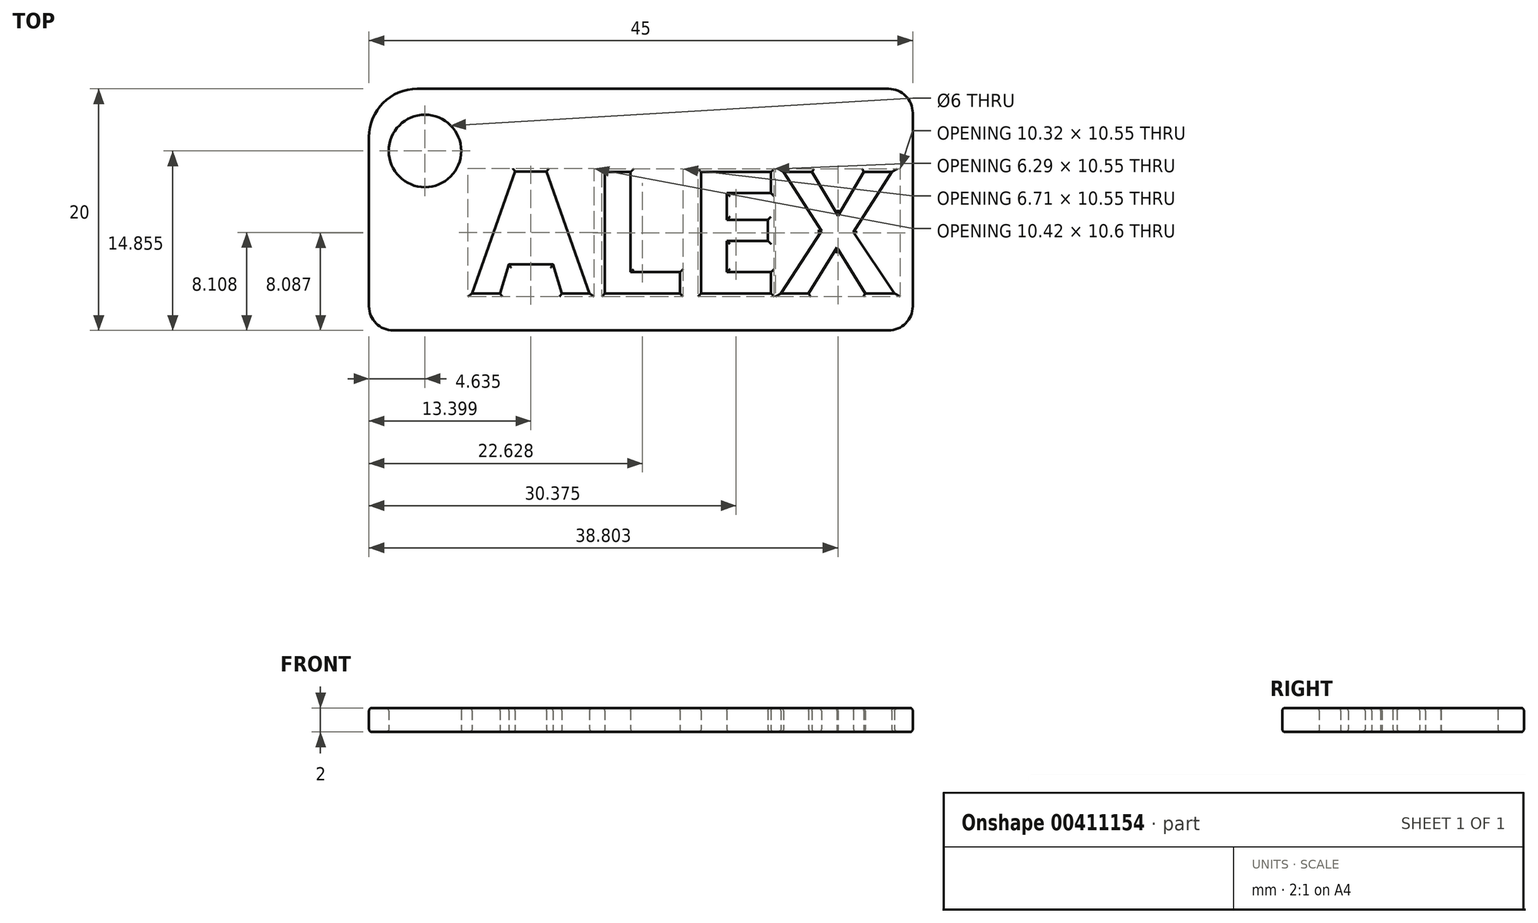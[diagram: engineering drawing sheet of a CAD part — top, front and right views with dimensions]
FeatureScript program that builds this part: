
annotation { "Feature Type Name" : "Feature", "Feature Type Description" : "" }
export const myFeature = defineFeature(function(context is Context, id is Id, definition is map)
    precondition{}
    {
        {
            var Q0;
            Q0=qCreatedBy(makeId("Top.planeOp"),FACE);
            var sketch = newSketch(context, id + "F0", { "sketchPlane" : qUnion([Q0])});
            skLineSegment(sketch, "E0.bottom", {"start": v(4, 0) * mm, "end": v(43, 0) * mm});
            skLineSegment(sketch, "E0.top", {"start": v(2, -20) * mm, "end": v(43, -20) * mm});
            skLineSegment(sketch, "E0.left", {"start": v(0, -4) * mm, "end": v(0, -18) * mm});
            skLineSegment(sketch, "E0.right", {"start": v(45, -2) * mm, "end": v(45, -18) * mm});
            skCircle(sketch, "E1", {"center": v(4.63, -5.15) * mm, "radius": 3 * mm});
            skText(sketch, "E2", { "text": "ALEX", "fontName": "OpenSans-Bold.ttf"});
            skPoint(sketch, "E3.visualSharp", {"position": v(0, 0) * mm});
            skArc(sketch, "E3.filletArc", {"start": v(4, 0) * mm, "mid": v(1.17, -1.17) * mm, "end": v(0, -4) * mm});
            skPoint(sketch, "E4.visualSharp", {"position": v(0, -20) * mm});
            skArc(sketch, "E4.filletArc", {"start": v(0, -18) * mm, "mid": v(0.59, -19.41) * mm, "end": v(2, -20) * mm});
            skPoint(sketch, "E5.visualSharp", {"position": v(45, -20) * mm});
            skArc(sketch, "E5.filletArc", {"start": v(43, -20) * mm, "mid": v(44.41, -19.41) * mm, "end": v(45, -18) * mm});
            skPoint(sketch, "E6.visualSharp", {"position": v(45, 0) * mm});
            skArc(sketch, "E6.filletArc", {"start": v(45, -2) * mm, "mid": v(44.41, -0.59) * mm, "end": v(43, 0) * mm});
            skLineSegment(sketch, "E7", {"start": v(12, -6.8) * mm, "end": v(13.42, -8.68) * mm});
            const initialGuessF0  = {"E2": [0.00854, -0.01694, 1, 0, 0.01014]};
            skSetInitialGuess(sketch, initialGuessF0);
            skSolve(sketch);
        }
        {
            var Q0;
            Q0=makeQuery(id+"F0.imprint","IMPRINT",FACE,{"disambiguationData":[TD([[makeQuery(id+"F0.imprint","IMPRINT",EDGE,{"derivedFrom":sQuery(id+"F0.wireOp",EDGE,"E0.bottom")}),-1.0]])]});
            extrude(context, id + "F1", {"entities" : qUnion([Q0]), "depth" : 2 * mm});
        }
        {
            var Q0;
            Q0=makeQuery(id+"F1.opExtrude","CAP_FACE",FACE,{"disambiguationData":[OSD([sQuery(id+"F0.wireOp",EDGE,"E0.bottom"),sQuery(id+"F0.wireOp",EDGE,"E0.top"),sQuery(id+"F0.wireOp",EDGE,"E0.left"),sQuery(id+"F0.wireOp",EDGE,"E0.right"),sQuery(id+"F0.wireOp",EDGE,"E1"),sQuery(id+"F0.wireOp",EDGE,"E2.sketch_text.stroke-0"),sQuery(id+"F0.wireOp",EDGE,"E2.sketch_text.stroke-1"),sQuery(id+"F0.wireOp",EDGE,"E2.sketch_text.stroke-2"),sQuery(id+"F0.wireOp",EDGE,"E2.sketch_text.stroke-3"),sQuery(id+"F0.wireOp",EDGE,"E2.sketch_text.stroke-4"),sQuery(id+"F0.wireOp",EDGE,"E2.sketch_text.stroke-5"),sQuery(id+"F0.wireOp",EDGE,"E2.sketch_text.stroke-6"),sQuery(id+"F0.wireOp",EDGE,"E2.sketch_text.stroke-7"),sQuery(id+"F0.wireOp",EDGE,"E2.sketch_text.stroke-12"),sQuery(id+"F0.wireOp",EDGE,"E2.sketch_text.stroke-13"),sQuery(id+"F0.wireOp",EDGE,"E2.sketch_text.stroke-14"),sQuery(id+"F0.wireOp",EDGE,"E2.sketch_text.stroke-15"),sQuery(id+"F0.wireOp",EDGE,"E2.sketch_text.stroke-16"),sQuery(id+"F0.wireOp",EDGE,"E2.sketch_text.stroke-17"),sQuery(id+"F0.wireOp",EDGE,"E2.sketch_text.stroke-18"),sQuery(id+"F0.wireOp",EDGE,"E2.sketch_text.stroke-19"),sQuery(id+"F0.wireOp",EDGE,"E2.sketch_text.stroke-20"),sQuery(id+"F0.wireOp",EDGE,"E2.sketch_text.stroke-21"),sQuery(id+"F0.wireOp",EDGE,"E2.sketch_text.stroke-22"),sQuery(id+"F0.wireOp",EDGE,"E2.sketch_text.stroke-23"),sQuery(id+"F0.wireOp",EDGE,"E2.sketch_text.stroke-24"),sQuery(id+"F0.wireOp",EDGE,"E2.sketch_text.stroke-25"),sQuery(id+"F0.wireOp",EDGE,"E2.sketch_text.stroke-26"),sQuery(id+"F0.wireOp",EDGE,"E2.sketch_text.stroke-27"),sQuery(id+"F0.wireOp",EDGE,"E2.sketch_text.stroke-28"),sQuery(id+"F0.wireOp",EDGE,"E2.sketch_text.stroke-29"),sQuery(id+"F0.wireOp",EDGE,"E2.sketch_text.stroke-30"),sQuery(id+"F0.wireOp",EDGE,"E2.sketch_text.stroke-31"),sQuery(id+"F0.wireOp",EDGE,"E2.sketch_text.stroke-32"),sQuery(id+"F0.wireOp",EDGE,"E2.sketch_text.stroke-33"),sQuery(id+"F0.wireOp",EDGE,"E2.sketch_text.stroke-34"),sQuery(id+"F0.wireOp",EDGE,"E2.sketch_text.stroke-35"),sQuery(id+"F0.wireOp",EDGE,"E2.sketch_text.stroke-36"),sQuery(id+"F0.wireOp",EDGE,"E2.sketch_text.stroke-37"),sQuery(id+"F0.wireOp",EDGE,"E2.sketch_text.stroke-38"),sQuery(id+"F0.wireOp",EDGE,"E2.sketch_text.stroke-39"),sQuery(id+"F0.wireOp",EDGE,"E2.sketch_text.stroke-40"),sQuery(id+"F0.wireOp",EDGE,"E2.sketch_text.stroke-41"),sQuery(id+"F0.wireOp",EDGE,"E3.filletArc"),sQuery(id+"F0.wireOp",EDGE,"E4.filletArc"),sQuery(id+"F0.wireOp",EDGE,"E5.filletArc"),sQuery(id+"F0.wireOp",EDGE,"E6.filletArc")])],"isStart":false});
            var Q1;
            Q1=makeQuery(id+"F1.opExtrude","CAP_FACE",FACE,{"disambiguationData":[OSD([sQuery(id+"F0.wireOp",EDGE,"E0.bottom"),sQuery(id+"F0.wireOp",EDGE,"E0.top"),sQuery(id+"F0.wireOp",EDGE,"E0.left"),sQuery(id+"F0.wireOp",EDGE,"E0.right"),sQuery(id+"F0.wireOp",EDGE,"E1"),sQuery(id+"F0.wireOp",EDGE,"E2.sketch_text.stroke-0"),sQuery(id+"F0.wireOp",EDGE,"E2.sketch_text.stroke-1"),sQuery(id+"F0.wireOp",EDGE,"E2.sketch_text.stroke-2"),sQuery(id+"F0.wireOp",EDGE,"E2.sketch_text.stroke-3"),sQuery(id+"F0.wireOp",EDGE,"E2.sketch_text.stroke-4"),sQuery(id+"F0.wireOp",EDGE,"E2.sketch_text.stroke-5"),sQuery(id+"F0.wireOp",EDGE,"E2.sketch_text.stroke-6"),sQuery(id+"F0.wireOp",EDGE,"E2.sketch_text.stroke-7"),sQuery(id+"F0.wireOp",EDGE,"E2.sketch_text.stroke-12"),sQuery(id+"F0.wireOp",EDGE,"E2.sketch_text.stroke-13"),sQuery(id+"F0.wireOp",EDGE,"E2.sketch_text.stroke-14"),sQuery(id+"F0.wireOp",EDGE,"E2.sketch_text.stroke-15"),sQuery(id+"F0.wireOp",EDGE,"E2.sketch_text.stroke-16"),sQuery(id+"F0.wireOp",EDGE,"E2.sketch_text.stroke-17"),sQuery(id+"F0.wireOp",EDGE,"E2.sketch_text.stroke-18"),sQuery(id+"F0.wireOp",EDGE,"E2.sketch_text.stroke-19"),sQuery(id+"F0.wireOp",EDGE,"E2.sketch_text.stroke-20"),sQuery(id+"F0.wireOp",EDGE,"E2.sketch_text.stroke-21"),sQuery(id+"F0.wireOp",EDGE,"E2.sketch_text.stroke-22"),sQuery(id+"F0.wireOp",EDGE,"E2.sketch_text.stroke-23"),sQuery(id+"F0.wireOp",EDGE,"E2.sketch_text.stroke-24"),sQuery(id+"F0.wireOp",EDGE,"E2.sketch_text.stroke-25"),sQuery(id+"F0.wireOp",EDGE,"E2.sketch_text.stroke-26"),sQuery(id+"F0.wireOp",EDGE,"E2.sketch_text.stroke-27"),sQuery(id+"F0.wireOp",EDGE,"E2.sketch_text.stroke-28"),sQuery(id+"F0.wireOp",EDGE,"E2.sketch_text.stroke-29"),sQuery(id+"F0.wireOp",EDGE,"E2.sketch_text.stroke-30"),sQuery(id+"F0.wireOp",EDGE,"E2.sketch_text.stroke-31"),sQuery(id+"F0.wireOp",EDGE,"E2.sketch_text.stroke-32"),sQuery(id+"F0.wireOp",EDGE,"E2.sketch_text.stroke-33"),sQuery(id+"F0.wireOp",EDGE,"E2.sketch_text.stroke-34"),sQuery(id+"F0.wireOp",EDGE,"E2.sketch_text.stroke-35"),sQuery(id+"F0.wireOp",EDGE,"E2.sketch_text.stroke-36"),sQuery(id+"F0.wireOp",EDGE,"E2.sketch_text.stroke-37"),sQuery(id+"F0.wireOp",EDGE,"E2.sketch_text.stroke-38"),sQuery(id+"F0.wireOp",EDGE,"E2.sketch_text.stroke-39"),sQuery(id+"F0.wireOp",EDGE,"E2.sketch_text.stroke-40"),sQuery(id+"F0.wireOp",EDGE,"E2.sketch_text.stroke-41"),sQuery(id+"F0.wireOp",EDGE,"E3.filletArc"),sQuery(id+"F0.wireOp",EDGE,"E4.filletArc"),sQuery(id+"F0.wireOp",EDGE,"E5.filletArc"),sQuery(id+"F0.wireOp",EDGE,"E6.filletArc")])],"isStart":true});
            fillet(context, id + "F2", {"entities" : qUnion([Q0, Q1]), "radius" : .25 * mm, "tangentPropagation" : true, "allowEdgeOverflow" : false});
        }
    });
